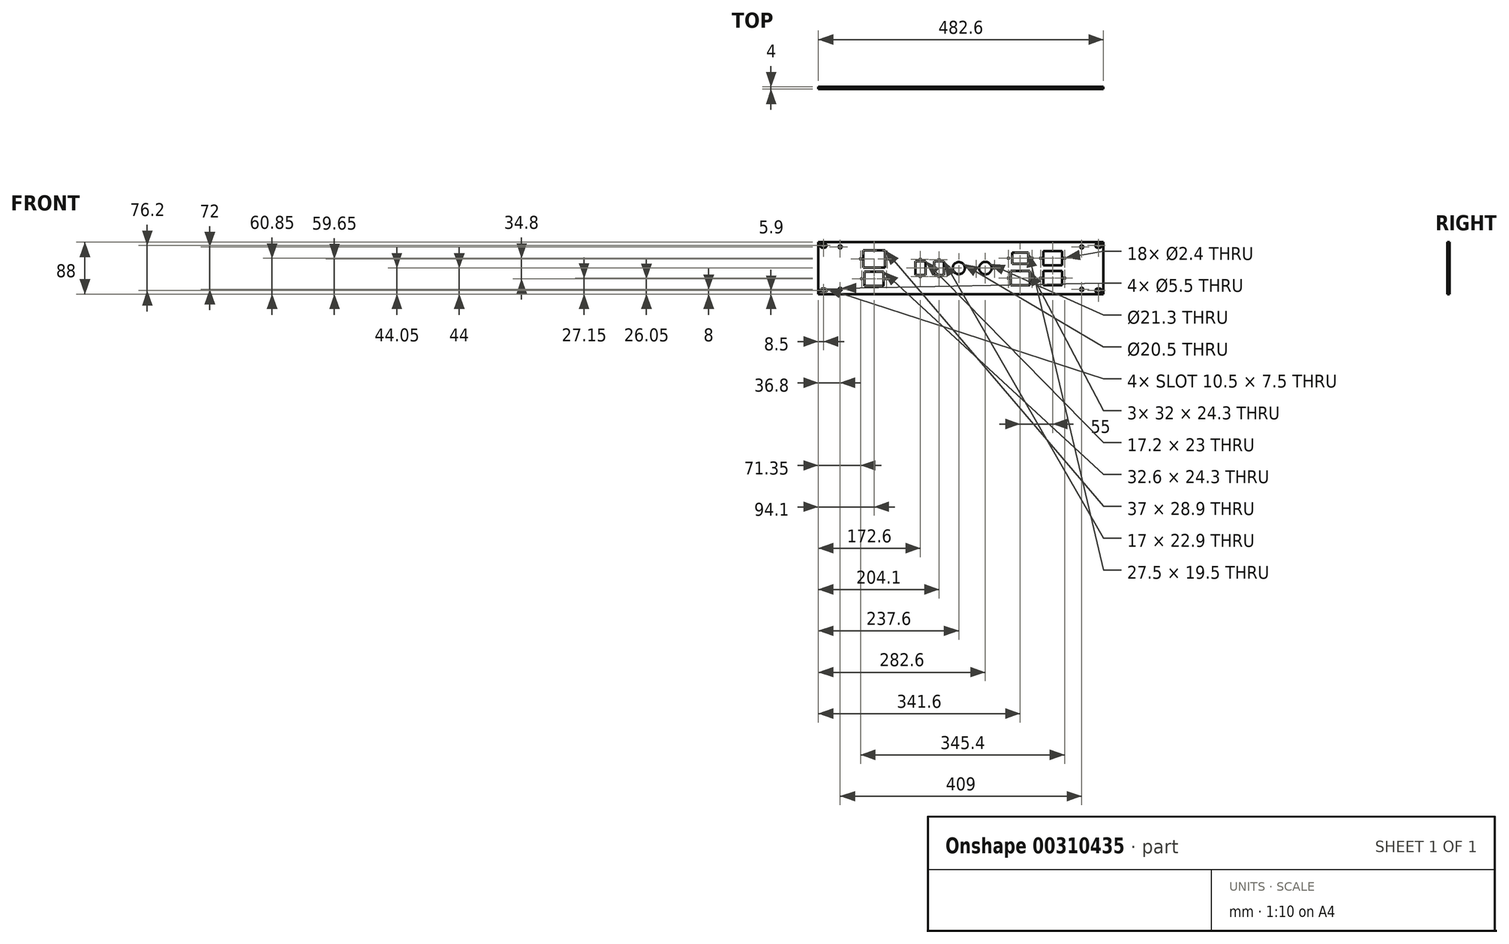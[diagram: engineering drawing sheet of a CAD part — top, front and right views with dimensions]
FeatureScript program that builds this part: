
annotation { "Feature Type Name" : "Feature", "Feature Type Description" : "" }
export const myFeature = defineFeature(function(context is Context, id is Id, definition is map)
    precondition{}
    {
        {
            var Q0;
            Q0=qCreatedBy(makeId("Front.planeOp"),FACE);
            var sketch = newSketch(context, id + "F0", { "sketchPlane" : qUnion([Q0])});
            skLineSegment(sketch, "E0.bottom", {"start": v(-482.6, 88) * mm, "end": v(0, 88) * mm});
            skLineSegment(sketch, "E0.top", {"start": v(-482.6, 0) * mm, "end": v(0, 0) * mm});
            skLineSegment(sketch, "E0.left", {"start": v(-482.6, 88) * mm, "end": v(-482.6, 0) * mm});
            skLineSegment(sketch, "E0.right", {"start": v(0, 88) * mm, "end": v(0, 0) * mm});
            skLineSegment(sketch, "E1.bottom", {"start": v(-102, 39.3) * mm, "end": v(-70, 39.3) * mm});
            skLineSegment(sketch, "E1.top", {"start": v(-102, 15) * mm, "end": v(-70, 15) * mm});
            skLineSegment(sketch, "E1.left", {"start": v(-102, 39.3) * mm, "end": v(-102, 15) * mm});
            skLineSegment(sketch, "E1.right", {"start": v(-70, 39.3) * mm, "end": v(-70, 15) * mm});
            skCircle(sketch, "E2", {"center": v(-200, 44) * mm, "radius": 10.65 * mm});
            skPoint(sketch, "E3", {"position": v(-215.4, 44) * mm});
            skPoint(sketch, "E4", {"position": v(-184.6, 44) * mm});
            skLineSegment(sketch, "E5.bottom", {"start": v(-154.75, 70.6) * mm, "end": v(-127.25, 70.6) * mm});
            skLineSegment(sketch, "E5.top", {"start": v(-154.75, 51.1) * mm, "end": v(-127.25, 51.1) * mm});
            skLineSegment(sketch, "E5.left", {"start": v(-154.75, 70.6) * mm, "end": v(-154.75, 51.1) * mm});
            skLineSegment(sketch, "E5.right", {"start": v(-127.25, 70.6) * mm, "end": v(-127.25, 51.1) * mm});
            skPoint(sketch, "E6", {"position": v(-161, 60.85) * mm});
            skPoint(sketch, "E7", {"position": v(-121, 60.85) * mm});
            skPoint(sketch, "E7.positionSnap0", {"position": v(-127.25, 60.85) * mm});
            skCircle(sketch, "E8", {"center": v(-245, 44) * mm, "radius": 10.25 * mm});
            skLineSegment(sketch, "E9.bottom", {"start": v(-287, 55.45) * mm, "end": v(-270, 55.45) * mm});
            skLineSegment(sketch, "E9.top", {"start": v(-287, 32.55) * mm, "end": v(-270, 32.55) * mm});
            skLineSegment(sketch, "E9.left", {"start": v(-287, 55.45) * mm, "end": v(-287, 32.55) * mm});
            skLineSegment(sketch, "E9.right", {"start": v(-270, 55.45) * mm, "end": v(-270, 32.55) * mm});
            skLineSegment(sketch, "E10.bottom", {"start": v(-102, 73) * mm, "end": v(-70, 73) * mm});
            skLineSegment(sketch, "E10.top", {"start": v(-102, 48.7) * mm, "end": v(-70, 48.7) * mm});
            skLineSegment(sketch, "E10.left", {"start": v(-102, 73) * mm, "end": v(-102, 48.7) * mm});
            skLineSegment(sketch, "E10.right", {"start": v(-70, 73) * mm, "end": v(-70, 48.7) * mm});
            skLineSegment(sketch, "E11.bottom", {"start": v(-407, 74.1) * mm, "end": v(-370, 74.1) * mm});
            skLineSegment(sketch, "E11.top", {"start": v(-407, 45.2) * mm, "end": v(-370, 45.2) * mm});
            skLineSegment(sketch, "E11.left", {"start": v(-407, 74.1) * mm, "end": v(-407, 45.2) * mm});
            skLineSegment(sketch, "E11.right", {"start": v(-370, 74.1) * mm, "end": v(-370, 45.2) * mm});
            skLineSegment(sketch, "E12.bottom", {"start": v(-404.8, 38.2) * mm, "end": v(-372.2, 38.2) * mm});
            skLineSegment(sketch, "E12.top", {"start": v(-404.8, 13.9) * mm, "end": v(-372.2, 13.9) * mm});
            skLineSegment(sketch, "E12.left", {"start": v(-404.8, 38.2) * mm, "end": v(-404.8, 13.9) * mm});
            skLineSegment(sketch, "E12.right", {"start": v(-372.2, 38.2) * mm, "end": v(-372.2, 13.9) * mm});
            skPoint(sketch, "E13", {"position": v(-278.5, 58.45) * mm});
            skPoint(sketch, "E14", {"position": v(-278.5, 29.55) * mm});
            skPoint(sketch, "E15", {"position": v(-411.25, 59.65) * mm});
            skPoint(sketch, "E16", {"position": v(-365.75, 59.65) * mm});
            skPoint(sketch, "E17", {"position": v(-409.55, 26.05) * mm});
            skPoint(sketch, "E17.positionSnap0", {"position": v(-404.8, 26.05) * mm});
            skPoint(sketch, "E18", {"position": v(-367.45, 26.05) * mm});
            skPoint(sketch, "E18.positionSnap0", {"position": v(-372.2, 26.05) * mm});
            skPoint(sketch, "E19", {"position": v(-445.8, 80) * mm});
            skPoint(sketch, "E20", {"position": v(-445.8, 8) * mm});
            skPoint(sketch, "E21", {"position": v(-36.8, 8) * mm});
            skPoint(sketch, "E22", {"position": v(-36.8, 80) * mm});
            skPoint(sketch, "E23", {"position": v(-474.1, 82.1) * mm});
            skPoint(sketch, "E24", {"position": v(-474.1, 5.9) * mm});
            skPoint(sketch, "E25", {"position": v(-8.5, 5.9) * mm});
            skPoint(sketch, "E26", {"position": v(-8.5, 82.1) * mm});
            skArc(sketch, "E27", {"start": v(-10, 9.65) * mm, "mid": v(-13.75, 5.9) * mm, "end": v(-10, 2.15) * mm});
            skArc(sketch, "E28", {"start": v(-7, 2.15) * mm, "mid": v(-3.25, 5.9) * mm, "end": v(-7, 9.65) * mm});
            skLineSegment(sketch, "E29", {"start": v(-10, 9.65) * mm, "end": v(-7, 9.65) * mm});
            skLineSegment(sketch, "E30", {"start": v(-10, 2.15) * mm, "end": v(-7, 2.15) * mm});
            skArc(sketch, "E31", {"start": v(-10, 85.85) * mm, "mid": v(-13.75, 82.1) * mm, "end": v(-10, 78.35) * mm});
            skArc(sketch, "E32", {"start": v(-7, 78.35) * mm, "mid": v(-3.25, 82.1) * mm, "end": v(-7, 85.85) * mm});
            skLineSegment(sketch, "E33", {"start": v(-10, 85.85) * mm, "end": v(-7, 85.85) * mm});
            skLineSegment(sketch, "E34", {"start": v(-10, 78.35) * mm, "end": v(-7, 78.35) * mm});
            skArc(sketch, "E35", {"start": v(-475.6, 85.85) * mm, "mid": v(-479.35, 82.1) * mm, "end": v(-475.6, 78.35) * mm});
            skArc(sketch, "E36", {"start": v(-472.6, 78.35) * mm, "mid": v(-468.85, 82.1) * mm, "end": v(-472.6, 85.85) * mm});
            skLineSegment(sketch, "E37", {"start": v(-475.6, 85.85) * mm, "end": v(-472.6, 85.85) * mm});
            skLineSegment(sketch, "E38", {"start": v(-475.6, 78.35) * mm, "end": v(-472.6, 78.35) * mm});
            skArc(sketch, "E39", {"start": v(-475.6, 9.65) * mm, "mid": v(-479.35, 5.9) * mm, "end": v(-475.6, 2.15) * mm});
            skArc(sketch, "E40", {"start": v(-472.6, 2.15) * mm, "mid": v(-468.85, 5.9) * mm, "end": v(-472.6, 9.65) * mm});
            skLineSegment(sketch, "E41", {"start": v(-475.6, 9.65) * mm, "end": v(-472.6, 9.65) * mm});
            skLineSegment(sketch, "E42", {"start": v(-475.6, 2.15) * mm, "end": v(-472.6, 2.15) * mm});
            skPoint(sketch, "E43", {"position": v(-106.15, 60.85) * mm});
            skPoint(sketch, "E44", {"position": v(-65.85, 60.85) * mm});
            skPoint(sketch, "E45", {"position": v(-65.85, 27.15) * mm});
            skPoint(sketch, "E46", {"position": v(-106.15, 27.15) * mm});
            skPoint(sketch, "E47", {"position": v(-388.5, 74.1) * mm});
            skLineSegment(sketch, "E48.bottom", {"start": v(-318.6, 55.55) * mm, "end": v(-301.4, 55.55) * mm});
            skLineSegment(sketch, "E48.top", {"start": v(-318.6, 32.55) * mm, "end": v(-301.4, 32.55) * mm});
            skLineSegment(sketch, "E48.left", {"start": v(-318.6, 55.55) * mm, "end": v(-318.6, 32.55) * mm});
            skLineSegment(sketch, "E48.right", {"start": v(-301.4, 55.55) * mm, "end": v(-301.4, 32.55) * mm});
            skPoint(sketch, "E49", {"position": v(-310, 58.8) * mm});
            skPoint(sketch, "E49.positionSnap0", {"position": v(-310, 55.55) * mm});
            skPoint(sketch, "E50", {"position": v(-310, 29.8) * mm});
            skPoint(sketch, "E50.positionSnap0", {"position": v(-310, 32.55) * mm});
            skLineSegment(sketch, "E51.bottom", {"start": v(-157, 39.3) * mm, "end": v(-125, 39.3) * mm});
            skLineSegment(sketch, "E51.top", {"start": v(-157, 15) * mm, "end": v(-125, 15) * mm});
            skLineSegment(sketch, "E51.left", {"start": v(-157, 39.3) * mm, "end": v(-157, 15) * mm});
            skLineSegment(sketch, "E51.right", {"start": v(-125, 39.3) * mm, "end": v(-125, 15) * mm});
            skPoint(sketch, "E52", {"position": v(-161.15, 27.15) * mm});
            skPoint(sketch, "E53", {"position": v(-120.85, 27.15) * mm});
            skSolve(sketch);
        }
        {
            var Q0;
            Q0=makeQuery(id+"F0.imprint","IMPRINT",FACE,{"disambiguationData":[TD([[makeQuery(id+"F0.imprint","IMPRINT",EDGE,{"derivedFrom":sQuery(id+"F0.wireOp",EDGE,"E0.bottom")}),-1.0]])]});
            extrude(context, id + "F1", {"entities" : qUnion([Q0]), "depth" : 4 * mm});
        }
        {
            var Q0;
            Q0=sQuery(id+"F0.wireOp",VERTEX,"E19");
            var Q1;
            Q1=sQuery(id+"F0.wireOp",VERTEX,"E20");
            var Q2;
            Q2=sQuery(id+"F0.wireOp",VERTEX,"E22");
            var Q3;
            Q3=sQuery(id+"F0.wireOp",VERTEX,"E21");
            var Q4;
            Q4=makeQuery(id+"F1.opExtrude","SWEPT_BODY",BODY,{"disambiguationData":[OSD([sQuery(id+"F0.wireOp",EDGE,"E0.bottom"),sQuery(id+"F0.wireOp",EDGE,"E0.top"),sQuery(id+"F0.wireOp",EDGE,"E0.left"),sQuery(id+"F0.wireOp",EDGE,"E0.right"),sQuery(id+"F0.wireOp",EDGE,"E1.bottom"),sQuery(id+"F0.wireOp",EDGE,"E1.top"),sQuery(id+"F0.wireOp",EDGE,"E1.left"),sQuery(id+"F0.wireOp",EDGE,"E1.right"),sQuery(id+"F0.wireOp",EDGE,"E2"),sQuery(id+"F0.wireOp",EDGE,"E5.bottom"),sQuery(id+"F0.wireOp",EDGE,"E5.top"),sQuery(id+"F0.wireOp",EDGE,"E5.left"),sQuery(id+"F0.wireOp",EDGE,"E5.right"),sQuery(id+"F0.wireOp",EDGE,"E8"),sQuery(id+"F0.wireOp",EDGE,"E9.bottom"),sQuery(id+"F0.wireOp",EDGE,"E9.top"),sQuery(id+"F0.wireOp",EDGE,"E9.left"),sQuery(id+"F0.wireOp",EDGE,"E9.right"),sQuery(id+"F0.wireOp",EDGE,"E10.bottom"),sQuery(id+"F0.wireOp",EDGE,"E10.top"),sQuery(id+"F0.wireOp",EDGE,"E10.left"),sQuery(id+"F0.wireOp",EDGE,"E10.right"),sQuery(id+"F0.wireOp",EDGE,"E11.bottom"),sQuery(id+"F0.wireOp",EDGE,"E11.top"),sQuery(id+"F0.wireOp",EDGE,"E11.left"),sQuery(id+"F0.wireOp",EDGE,"E11.right"),sQuery(id+"F0.wireOp",EDGE,"E12.bottom"),sQuery(id+"F0.wireOp",EDGE,"E12.top"),sQuery(id+"F0.wireOp",EDGE,"E12.left"),sQuery(id+"F0.wireOp",EDGE,"E12.right"),sQuery(id+"F0.wireOp",EDGE,"E27"),sQuery(id+"F0.wireOp",EDGE,"E28"),sQuery(id+"F0.wireOp",EDGE,"E29"),sQuery(id+"F0.wireOp",EDGE,"E30"),sQuery(id+"F0.wireOp",EDGE,"E31"),sQuery(id+"F0.wireOp",EDGE,"E32"),sQuery(id+"F0.wireOp",EDGE,"E33"),sQuery(id+"F0.wireOp",EDGE,"E34"),sQuery(id+"F0.wireOp",EDGE,"E35"),sQuery(id+"F0.wireOp",EDGE,"E36"),sQuery(id+"F0.wireOp",EDGE,"E37"),sQuery(id+"F0.wireOp",EDGE,"E38"),sQuery(id+"F0.wireOp",EDGE,"E39"),sQuery(id+"F0.wireOp",EDGE,"E40"),sQuery(id+"F0.wireOp",EDGE,"E41"),sQuery(id+"F0.wireOp",EDGE,"E42")])]});
            hole(context, id + "F2", {"style" : HoleStyle.SIMPLE, "endStyle" : HoleEndStyle.THROUGH, "oppositeDirection" : true, "holeDiameter" : 5.5 * mm, "tappedDepth" : 12 * mm, "tapClearance" : 3, "locations" : qUnion([Q0, Q1, Q2, Q3]), "scope" : qUnion([Q4])});
        }
        {
            var Q0;
            Q0=sQuery(id+"F0.wireOp",VERTEX,"E7");
            var Q1;
            Q1=sQuery(id+"F0.wireOp",VERTEX,"E4");
            var Q2;
            Q2=sQuery(id+"F0.wireOp",VERTEX,"E3");
            var Q3;
            Q3=sQuery(id+"F0.wireOp",VERTEX,"E6");
            var Q4;
            Q4=sQuery(id+"F0.wireOp",VERTEX,"E13");
            var Q5;
            Q5=sQuery(id+"F0.wireOp",VERTEX,"E14");
            var Q6;
            Q6=sQuery(id+"F0.wireOp",VERTEX,"E16");
            var Q7;
            Q7=sQuery(id+"F0.wireOp",VERTEX,"E15");
            var Q8;
            Q8=sQuery(id+"F0.wireOp",VERTEX,"E17");
            var Q9;
            Q9=sQuery(id+"F0.wireOp",VERTEX,"E18");
            var Q10;
            Q10=sQuery(id+"F0.wireOp",VERTEX,"E43");
            var Q11;
            Q11=sQuery(id+"F0.wireOp",VERTEX,"E44");
            var Q12;
            Q12=sQuery(id+"F0.wireOp",VERTEX,"E45");
            var Q13;
            Q13=sQuery(id+"F0.wireOp",VERTEX,"E46");
            var Q14;
            Q14=sQuery(id+"F0.wireOp",VERTEX,"E49");
            var Q15;
            Q15=sQuery(id+"F0.wireOp",VERTEX,"E50");
            var Q16;
            Q16=sQuery(id+"F0.wireOp",VERTEX,"E52");
            var Q17;
            Q17=sQuery(id+"F0.wireOp",VERTEX,"E53");
            var Q18;
            Q18=makeQuery(id+"F1.opExtrude","SWEPT_BODY",BODY,{"disambiguationData":[OSD([sQuery(id+"F0.wireOp",EDGE,"E0.bottom"),sQuery(id+"F0.wireOp",EDGE,"E0.top"),sQuery(id+"F0.wireOp",EDGE,"E0.left"),sQuery(id+"F0.wireOp",EDGE,"E0.right"),sQuery(id+"F0.wireOp",EDGE,"E1.bottom"),sQuery(id+"F0.wireOp",EDGE,"E1.top"),sQuery(id+"F0.wireOp",EDGE,"E1.left"),sQuery(id+"F0.wireOp",EDGE,"E1.right"),sQuery(id+"F0.wireOp",EDGE,"E2"),sQuery(id+"F0.wireOp",EDGE,"E5.bottom"),sQuery(id+"F0.wireOp",EDGE,"E5.top"),sQuery(id+"F0.wireOp",EDGE,"E5.left"),sQuery(id+"F0.wireOp",EDGE,"E5.right"),sQuery(id+"F0.wireOp",EDGE,"E8"),sQuery(id+"F0.wireOp",EDGE,"E9.bottom"),sQuery(id+"F0.wireOp",EDGE,"E9.top"),sQuery(id+"F0.wireOp",EDGE,"E9.left"),sQuery(id+"F0.wireOp",EDGE,"E9.right"),sQuery(id+"F0.wireOp",EDGE,"E10.bottom"),sQuery(id+"F0.wireOp",EDGE,"E10.top"),sQuery(id+"F0.wireOp",EDGE,"E10.left"),sQuery(id+"F0.wireOp",EDGE,"E10.right"),sQuery(id+"F0.wireOp",EDGE,"E11.bottom"),sQuery(id+"F0.wireOp",EDGE,"E11.top"),sQuery(id+"F0.wireOp",EDGE,"E11.left"),sQuery(id+"F0.wireOp",EDGE,"E11.right"),sQuery(id+"F0.wireOp",EDGE,"E12.bottom"),sQuery(id+"F0.wireOp",EDGE,"E12.top"),sQuery(id+"F0.wireOp",EDGE,"E12.left"),sQuery(id+"F0.wireOp",EDGE,"E12.right"),sQuery(id+"F0.wireOp",EDGE,"E27"),sQuery(id+"F0.wireOp",EDGE,"E28"),sQuery(id+"F0.wireOp",EDGE,"E29"),sQuery(id+"F0.wireOp",EDGE,"E30"),sQuery(id+"F0.wireOp",EDGE,"E31"),sQuery(id+"F0.wireOp",EDGE,"E32"),sQuery(id+"F0.wireOp",EDGE,"E33"),sQuery(id+"F0.wireOp",EDGE,"E34"),sQuery(id+"F0.wireOp",EDGE,"E35"),sQuery(id+"F0.wireOp",EDGE,"E36"),sQuery(id+"F0.wireOp",EDGE,"E37"),sQuery(id+"F0.wireOp",EDGE,"E38"),sQuery(id+"F0.wireOp",EDGE,"E39"),sQuery(id+"F0.wireOp",EDGE,"E40"),sQuery(id+"F0.wireOp",EDGE,"E41"),sQuery(id+"F0.wireOp",EDGE,"E42")])]});
            hole(context, id + "F3", {"style" : HoleStyle.SIMPLE, "endStyle" : HoleEndStyle.THROUGH, "oppositeDirection" : true, "standardTappedOrClearance" : lookupTablePath({ "standard" : "ISO", "engagement" : "75%", "pitch" : "0.6 mm", "size" : "M3", "type" : "Tapped" }), "standardBlindInLast" : lookupTablePath({ "standard" : "ISO", "engagement" : "75%", "pitch" : "0.6 mm", "size" : "M3", "type" : "Tapped" }), "holeDiameter" : 2.4 * mm, "showTappedDepth" : true, "tappedDepth" : 12 * mm, "tapClearance" : 3, "locations" : qUnion([Q0, Q1, Q2, Q3, Q4, Q5, Q6, Q7, Q8, Q9, Q10, Q11, Q12, Q13, Q14, Q15, Q16, Q17]), "scope" : qUnion([Q18]), "majorDiameter" : 5 * mm});
        }
    });
